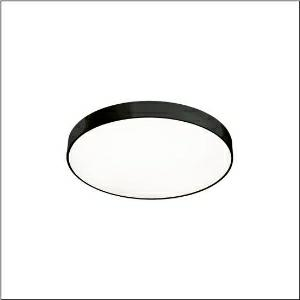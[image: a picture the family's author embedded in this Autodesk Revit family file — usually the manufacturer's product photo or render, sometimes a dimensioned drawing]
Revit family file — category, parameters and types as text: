
# Revit family: round_21_m_51mr36fd0421b
name_source: partatom
category: Lighting Fixtures
units: mm (PartAtom-declared; Revit-internal decimal feet)

## family parameters
Cut with Voids When Loaded = No
Host = Face
Light Source = No
Part Type = Normal
Room Calculation Point = No
Round Connector Dimension = Use Diameter
Shared = No

## types (1)
- Round 21 M (1 x LED, 7810 lm, 54.9 W, 4000K)
    Apparent Load = 55 VA
    CIE Flux Codes = 49 80 96 100 100
    Color Rendering = 80
    Color Temperature = 4000K
    Default Elevation = 1800 mm
    Description = Round 21 M, wall and ceiling luminaire, primary optical cover: cover, of PMMA, opal, light emission: direct distribution, primary light characteristic: symmetric, installation type: surface-mounted, suspended mounting, LED, rated luminous flux: 7.810lm, luminous efficacy: 142lm/W, light colour: 840, colour temperature: 4000K, control gear: DALI 2, with terminal, 5-pole, mains connection: 230V, AC, 50/60Hz, rated input power: 55W, housing, of aluminium, coated, black, diameter: 600mm, height: 62mm, protection rating (complete): IP40, insulation class (complete): insulation class I (protective earthing), certification: CE, impact resistance: IK04, permissible operating ambient temperature: -10..+35°C, packaging unit: 1 piece
    Height = 87 mm
    Lamp = 1 x LED
    Lamp Light Flux = 7810 lm
    Lamp Power = 54.9 W
    Lamp count = 1
    Length = 600 mm
    Luminous efficacy = 142 lm/W
    Manufacturer = Siteco
    ModVariant = No
    Model = 51MR36FD0421B
    Mounting Place = Ceiling
    Mounting Type = Surface mounted
    Number of Poles = 1
    OnlyDefault = Yes
    Power Factor = 1
    Product Name = Round 21 M
    Product group = wall and ceiling luminaire
    ProductGroupID = 304
    Protection Class = Protection class I
    Protection Degree = IP 40
    RLX_Detail_Level = 1
    RLX_Emergency_Light_Flux = 0 lm
    RLX_Emergency_Type = 0
    RLX_Emergency_Type_DB = No
    RlxData = <blob elided: 17733 chars, md5=f6fd453f>
    Socket = socket
    Standby Power = 0 W
    System Light Flux = 7810 lm
    System Power = 55 W
    Type Comments = Product without accessories
    Type Image = l_1258332.jpg
    URL = http://relux.com
    VarID = ---
    Voltage = 0 V
    Weight = 0.00 kg
    Width = 0 mm  [stored 0 ft]

note: [stored X ft] marks values corroborated as IEEE doubles in the binary element streams (Revit-internal decimal feet)

## geometry (parser evidence)
native form markers: Blend x4, Sweep x10
no freeform markers — native parametric forms only
